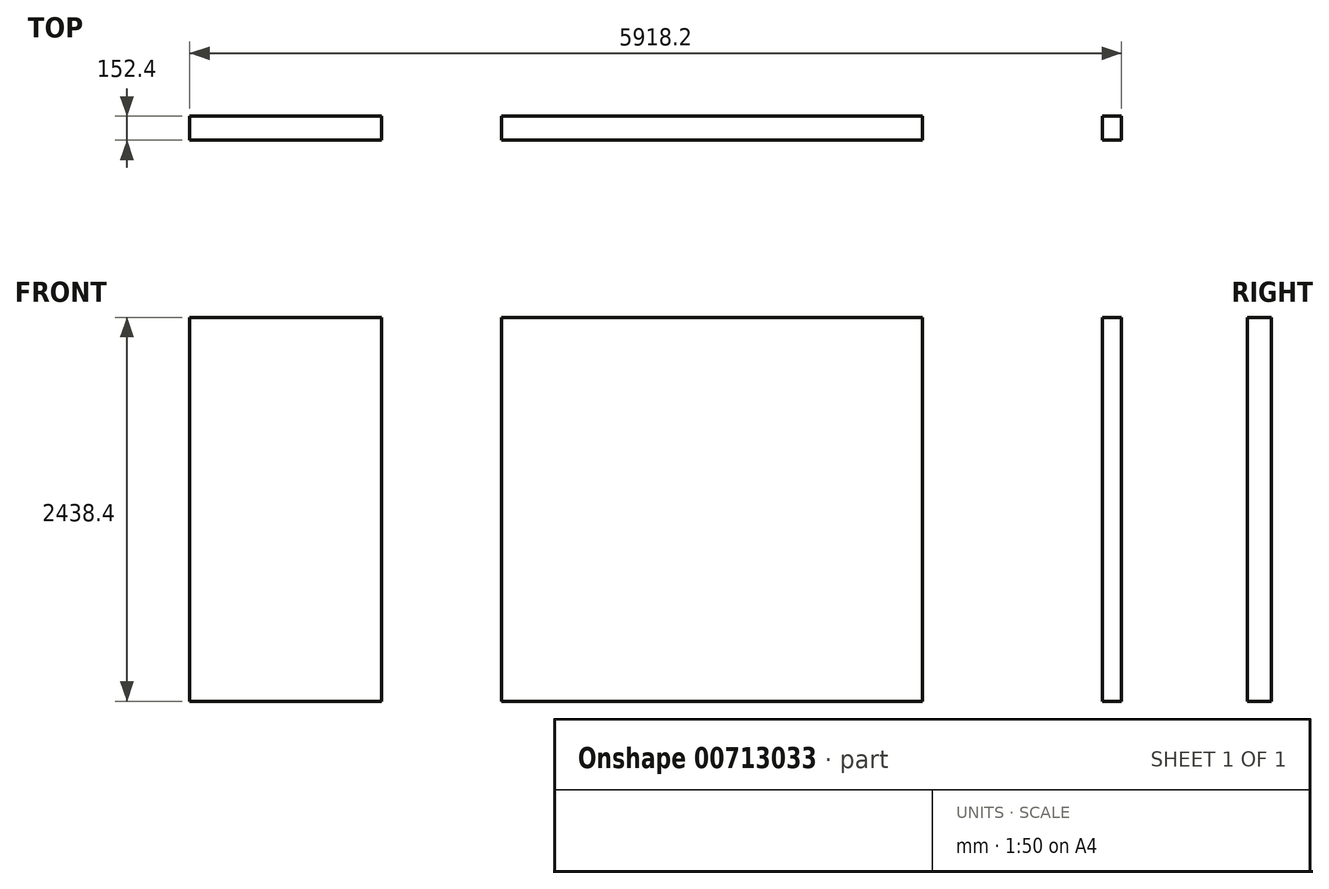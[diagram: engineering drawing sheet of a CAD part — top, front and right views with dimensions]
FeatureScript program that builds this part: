
annotation { "Feature Type Name" : "Feature", "Feature Type Description" : "" }
export const myFeature = defineFeature(function(context is Context, id is Id, definition is map)
    precondition{}
    {
        {
            var Q0;
            Q0=qCreatedBy(makeId("Top.planeOp"),FACE);
            var sketch = newSketch(context, id + "F0", { "sketchPlane" : qUnion([Q0])});
            skLineSegment(sketch, "E0.bottom", {"start": v(0, 0) * mm, "end": v(5918.2, 0) * mm});
            skLineSegment(sketch, "E0.top", {"start": v(0, 4057.65) * mm, "end": v(5918.2, 4057.65) * mm});
            skLineSegment(sketch, "E0.left", {"start": v(0, 0) * mm, "end": v(0, 4057.65) * mm});
            skLineSegment(sketch, "E0.right", {"start": v(5918.2, 0) * mm, "end": v(5918.2, 4057.65) * mm});
            skLineSegment(sketch, "E1.top", {"start": v(0, -152.4) * mm, "end": v(5918.2, -152.4) * mm});
            skLineSegment(sketch, "E1.left", {"start": v(0, 0) * mm, "end": v(0, -152.4) * mm});
            skLineSegment(sketch, "E1.right", {"start": v(5918.2, 0) * mm, "end": v(5918.2, -152.4) * mm});
            skLineSegment(sketch, "E2.bottom", {"start": v(1219.2, 0) * mm, "end": v(1981.2, 0) * mm});
            skLineSegment(sketch, "E2.top", {"start": v(1219.2, -152.4) * mm, "end": v(1981.2, -152.4) * mm});
            skLineSegment(sketch, "E2.left", {"start": v(1219.2, 0) * mm, "end": v(1219.2, -152.4) * mm});
            skLineSegment(sketch, "E2.right", {"start": v(1981.2, 0) * mm, "end": v(1981.2, -152.4) * mm});
            skLineSegment(sketch, "E3.bottom", {"start": v(5797.55, 0) * mm, "end": v(4654.55, 0) * mm});
            skLineSegment(sketch, "E3.top", {"start": v(5797.55, -152.4) * mm, "end": v(4654.55, -152.4) * mm});
            skLineSegment(sketch, "E3.left", {"start": v(5797.55, 0) * mm, "end": v(5797.55, -152.4) * mm});
            skLineSegment(sketch, "E3.right", {"start": v(4654.55, 0) * mm, "end": v(4654.55, -152.4) * mm});
            skSolve(sketch);
        }
        {
            var Q0;
            {var subQ0=sQuery(id+"F0.wireOp",EDGE,"E1.right");Q0=makeQuery(id+"F0.imprint","IMPRINT",FACE,{"disambiguationData":[TD([[makeQuery(id+"F0.imprint","IMPRINT",EDGE,{"derivedFrom":subQ0}),-1.0]])]});}
            var Q1;
            {var subQ0=sQuery(id+"F0.wireOp",EDGE,"E1.left");Q1=makeQuery(id+"F0.imprint","IMPRINT",FACE,{"disambiguationData":[TD([[makeQuery(id+"F0.imprint","IMPRINT",EDGE,{"derivedFrom":subQ0}),1.0]])]});}
            var Q2;
            {var subQ0=sQuery(id+"F0.wireOp",EDGE,"E2.right");Q2=makeQuery(id+"F0.imprint","IMPRINT",FACE,{"disambiguationData":[TD([[makeQuery(id+"F0.imprint","IMPRINT",EDGE,{"derivedFrom":subQ0}),1.0]])]});}
            extrude(context, id + "F1", {"entities" : qUnion([Q0, Q1, Q2]), "depth" : 2438.4 * mm, "offsetDistance" : 25.4 * mm});
        }
    });
